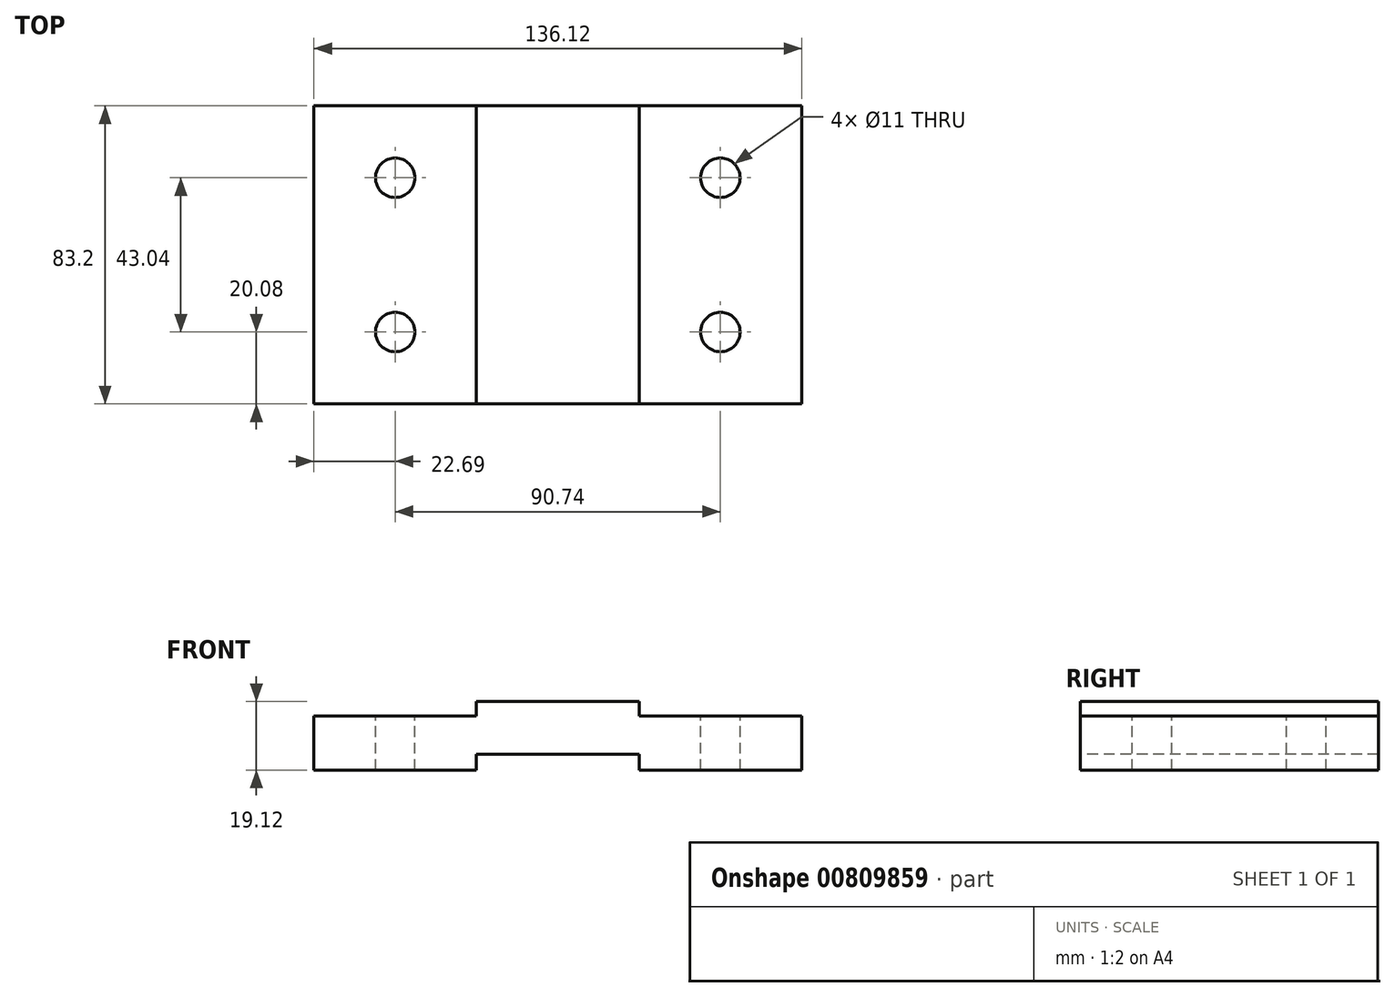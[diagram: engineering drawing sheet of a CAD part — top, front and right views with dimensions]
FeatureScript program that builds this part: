
annotation { "Feature Type Name" : "Feature", "Feature Type Description" : "" }
export const myFeature = defineFeature(function(context is Context, id is Id, definition is map)
    precondition{}
    {
        {
            var Q0;
            Q0=qCreatedBy(makeId("Front.planeOp"),FACE);
            var sketch = newSketch(context, id + "F0", { "sketchPlane" : qUnion([Q0])});
            skLineSegment(sketch, "E0", {"start": v(0, 0) * mm, "end": v(0, 15.08) * mm});
            skLineSegment(sketch, "E1", {"start": v(0, 15.08) * mm, "end": v(45.37, 15.08) * mm});
            skLineSegment(sketch, "E2", {"start": v(45.37, 15.08) * mm, "end": v(45.37, 19.12) * mm});
            skLineSegment(sketch, "E3", {"start": v(45.37, 19.12) * mm, "end": v(90.75, 19.12) * mm});
            skLineSegment(sketch, "E4", {"start": v(90.75, 19.12) * mm, "end": v(90.75, 15.08) * mm});
            skLineSegment(sketch, "E5", {"start": v(90.75, 15.08) * mm, "end": v(136.12, 15.08) * mm});
            skLineSegment(sketch, "E6", {"start": v(136.12, 15.08) * mm, "end": v(136.12, 0) * mm});
            skLineSegment(sketch, "E7", {"start": v(136.12, 0) * mm, "end": v(90.75, 0) * mm});
            skLineSegment(sketch, "E8", {"start": v(90.75, 0) * mm, "end": v(90.75, 4.35) * mm});
            skLineSegment(sketch, "E9", {"start": v(90.75, 4.35) * mm, "end": v(45.37, 4.35) * mm});
            skLineSegment(sketch, "E10", {"start": v(45.37, 4.35) * mm, "end": v(45.37, 0) * mm});
            skLineSegment(sketch, "E11", {"start": v(45.37, 0) * mm, "end": v(0, 0) * mm});
            skSolve(sketch);
        }
        {
            var Q0;
            Q0 = qSketchRegion(id + "F0", true);
            extrude(context, id + "F1", {"entities" : qUnion([Q0]), "oppositeDirection" : true, "depth" : 83.2 * mm, "offsetDistance" : 25 * mm});
        }
        {
            var Q0;
            Q0=qCreatedBy(makeId("Top.planeOp"),FACE);
            cPlane(context, id + "F2", {"entities" : qUnion([Q0]), "cplaneType" : CPlaneType.OFFSET, "offset" : 15.08 * mm, "width" : 150 * mm, "height" : 150 * mm});
        }
        {
            var Q0;
            Q0=qCreatedBy(id+"F2.planeOp",FACE);
            var sketch = newSketch(context, id + "F3", { "sketchPlane" : qUnion([Q0])});
            skPoint(sketch, "E12", {"position": v(22.7, 20.08) * mm});
            skPoint(sketch, "E13", {"position": v(22.7, 63.12) * mm});
            skPoint(sketch, "E14", {"position": v(113.43, 63.12) * mm});
            skPoint(sketch, "E15", {"position": v(113.43, 20.08) * mm});
            skSolve(sketch);
        }
        {
            var Q0;
            Q0=sQuery(id+"F3.wireOp",VERTEX,"E12");
            var Q1;
            Q1=sQuery(id+"F3.wireOp",VERTEX,"E13");
            var Q2;
            Q2=sQuery(id+"F3.wireOp",VERTEX,"E14");
            var Q3;
            Q3=sQuery(id+"F3.wireOp",VERTEX,"E15");
            var Q4;
            Q4=makeQuery(id+"F1.opExtrude","SWEPT_BODY",BODY,{"disambiguationData":[OSD([sQuery(id+"F0.wireOp",EDGE,"E0"),sQuery(id+"F0.wireOp",EDGE,"E1"),sQuery(id+"F0.wireOp",EDGE,"E2"),sQuery(id+"F0.wireOp",EDGE,"E3"),sQuery(id+"F0.wireOp",EDGE,"E4"),sQuery(id+"F0.wireOp",EDGE,"E5"),sQuery(id+"F0.wireOp",EDGE,"E6"),sQuery(id+"F0.wireOp",EDGE,"E7"),sQuery(id+"F0.wireOp",EDGE,"E8"),sQuery(id+"F0.wireOp",EDGE,"E9"),sQuery(id+"F0.wireOp",EDGE,"E10"),sQuery(id+"F0.wireOp",EDGE,"E11")])]});
            hole(context, id + "F4", {"style" : HoleStyle.SIMPLE, "endStyle" : HoleEndStyle.THROUGH, "holeDiameter" : 11 * mm, "majorDiameter" : 5 * mm, "isTappedThrough" : true, "tappedDepth" : 12 * mm, "tapClearance" : 3, "startFromSketch" : true, "locations" : qUnion([Q0, Q1, Q2, Q3]), "scope" : qUnion([Q4])});
        }
    });
